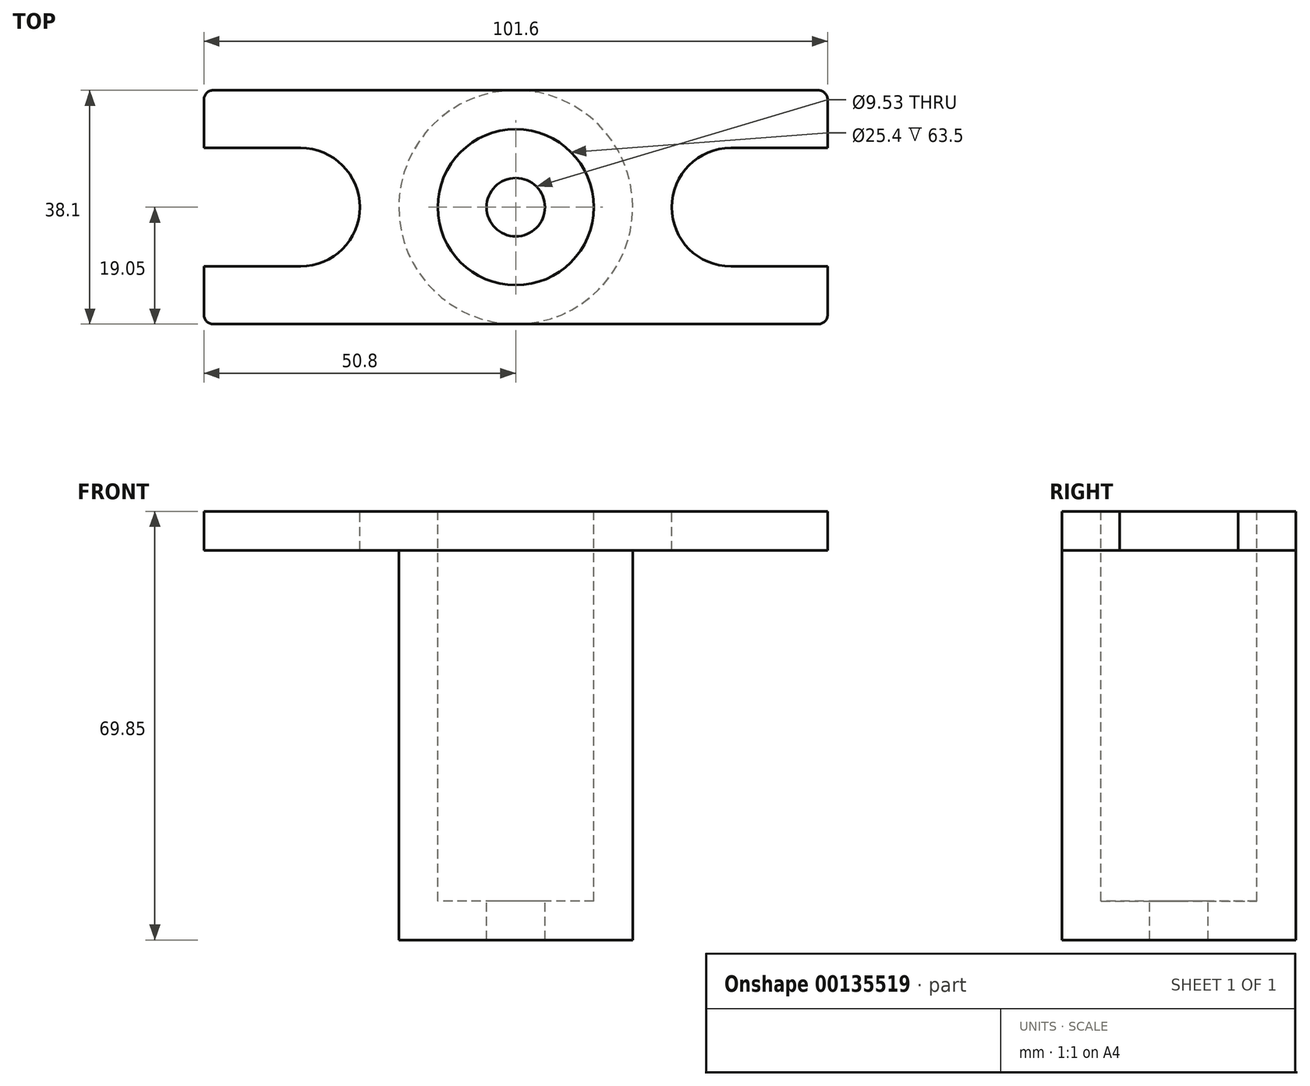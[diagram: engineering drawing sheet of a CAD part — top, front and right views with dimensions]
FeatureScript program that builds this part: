
annotation { "Feature Type Name" : "Feature", "Feature Type Description" : "" }
export const myFeature = defineFeature(function(context is Context, id is Id, definition is map)
    precondition{}
    {
        {
            var Q0;
            Q0=qCreatedBy(makeId("Top.planeOp"),FACE);
            var sketch = newSketch(context, id + "F0", { "sketchPlane" : qUnion([Q0])});
            skCircle(sketch, "E0", {"center": v(0, 0) * mm, "radius": 4.76 * mm});
            skCircle(sketch, "E1", {"center": v(0, 0) * mm, "radius": 19.05 * mm});
            skSolve(sketch);
        }
        {
            var Q0;
            Q0 = qSketchRegion(id + "F0", true);
            extrude(context, id + "F1", {"entities" : qUnion([Q0]), "oppositeDirection" : true, "depth" : 69.85 * mm});
        }
        {
            var Q0;
            Q0=makeQuery(id+"F1.opExtrude","CAP_FACE",FACE,{"disambiguationData":[OSD([sQuery(id+"F0.wireOp",EDGE,"E0"),sQuery(id+"F0.wireOp",EDGE,"E1")])],"isStart":true});
            var sketch = newSketch(context, id + "F2", { "sketchPlane" : qUnion([Q0])});
            skCircle(sketch, "E2", {"center": v(0, 0) * mm, "radius": 12.7 * mm});
            skSolve(sketch);
        }
        {
            var Q0;
            Q0 = qSketchRegion(id + "F2", true);
            extrude(context, id + "F3", {"entities" : qUnion([Q0]), "operationType" : NewBodyOperationType.REMOVE, "oppositeDirection" : true, "depth" : 63.5 * mm});
        }
        {
            var Q0;
            Q0=makeQuery(id+"F1.opExtrude","CAP_FACE",FACE,{"disambiguationData":[OSD([sQuery(id+"F0.wireOp",EDGE,"E0"),sQuery(id+"F0.wireOp",EDGE,"E1")])],"isStart":true});
            var sketch = newSketch(context, id + "F4", { "sketchPlane" : qUnion([Q0])});
            skLineSegment(sketch, "E3.bottom", {"start": v(49.28, -19.05) * mm, "end": v(-49.28, -19.05) * mm});
            skLineSegment(sketch, "E3.top", {"start": v(49.28, 19.05) * mm, "end": v(-49.28, 19.05) * mm});
            skLineSegment(sketch, "E3.left", {"start": v(50.8, -17.53) * mm, "end": v(50.8, 17.53) * mm});
            skLineSegment(sketch, "E3.right", {"start": v(-50.8, -17.53) * mm, "end": v(-50.8, 17.53) * mm});
            skPoint(sketch, "E3.middle", {"position": v(0, 0) * mm});
            skPoint(sketch, "E4.visualSharp", {"position": v(-50.8, 19.05) * mm});
            skArc(sketch, "E4.filletArc", {"start": v(-49.28, 19.05) * mm, "mid": v(-50.35, 18.6) * mm, "end": v(-50.8, 17.53) * mm});
            skPoint(sketch, "E5.visualSharp", {"position": v(50.8, 19.05) * mm});
            skArc(sketch, "E5.filletArc", {"start": v(50.8, 17.53) * mm, "mid": v(50.35, 18.6) * mm, "end": v(49.28, 19.05) * mm});
            skPoint(sketch, "E6.visualSharp", {"position": v(50.8, -19.05) * mm});
            skArc(sketch, "E6.filletArc", {"start": v(49.28, -19.05) * mm, "mid": v(50.35, -18.6) * mm, "end": v(50.8, -17.53) * mm});
            skPoint(sketch, "E7.visualSharp", {"position": v(-50.8, -19.05) * mm});
            skArc(sketch, "E7.filletArc", {"start": v(-50.8, -17.53) * mm, "mid": v(-50.35, -18.6) * mm, "end": v(-49.28, -19.05) * mm});
            skCircle(sketch, "E8", {"center": v(0, 0) * mm, "radius": 12.7 * mm});
            skSolve(sketch);
        }
        {
            var Q0;
            Q0 = qSketchRegion(id + "F4", true);
            extrude(context, id + "F5", {"entities" : qUnion([Q0]), "operationType" : NewBodyOperationType.ADD, "oppositeDirection" : true, "depth" : 6.35 * mm});
        }
        {
            var Q0;
            Q0=makeQuery(id+"F5.boolean.opBoolean","MERGE",FACE,{"derivedFrom":[makeQuery(id+"F1.opExtrude","CAP_FACE",FACE,{"disambiguationData":[OSD([sQuery(id+"F0.wireOp",EDGE,"E0"),sQuery(id+"F0.wireOp",EDGE,"E1")])],"isStart":true}),makeQuery(id+"F5.opExtrude","CAP_FACE",FACE,{"disambiguationData":[OSD([sQuery(id+"F4.wireOp",EDGE,"E3.bottom"),sQuery(id+"F4.wireOp",EDGE,"E3.top"),sQuery(id+"F4.wireOp",EDGE,"E3.left"),sQuery(id+"F4.wireOp",EDGE,"E3.right"),sQuery(id+"F4.wireOp",EDGE,"E4.filletArc"),sQuery(id+"F4.wireOp",EDGE,"E5.filletArc"),sQuery(id+"F4.wireOp",EDGE,"E6.filletArc"),sQuery(id+"F4.wireOp",EDGE,"E7.filletArc"),sQuery(id+"F4.wireOp",EDGE,"E8")])],"isStart":true})]});
            var sketch = newSketch(context, id + "F6", { "sketchPlane" : qUnion([Q0])});
            skLineSegment(sketch, "E9", {"start": v(0, 0) * mm, "end": v(-35.05, 0) * mm, "construction": true});
            skLineSegment(sketch, "E10", {"start": v(0, 0) * mm, "end": v(35.05, 0) * mm, "construction": true});
            skArc(sketch, "E11", {"start": v(-35.05, -9.65) * mm, "mid": v(-25.4, 0) * mm, "end": v(-35.05, 9.65) * mm});
            skArc(sketch, "E12", {"start": v(35.05, 9.65) * mm, "mid": v(25.4, 0) * mm, "end": v(35.05, -9.65) * mm});
            skLineSegment(sketch, "E13", {"start": v(-35.05, -9.65) * mm, "end": v(-50.8, -9.65) * mm});
            skLineSegment(sketch, "E14", {"start": v(-35.05, 9.65) * mm, "end": v(-50.8, 9.65) * mm});
            skLineSegment(sketch, "E15", {"start": v(35.05, -9.65) * mm, "end": v(50.8, -9.65) * mm});
            skLineSegment(sketch, "E16", {"start": v(35.05, 9.65) * mm, "end": v(50.8, 9.65) * mm});
            skLineSegment(sketch, "E17", {"start": v(50.8, 9.65) * mm, "end": v(50.8, -9.65) * mm});
            skSolve(sketch);
        }
        {
            var Q0;
            Q0=makeQuery(id+"F6.imprint","IMPRINT",FACE,{"disambiguationData":[TD([[makeQuery(id+"F6.imprint","IMPRINT",EDGE,{"derivedFrom":sQuery(id+"F6.wireOp",EDGE,"E12")}),1.0]])]});
            var Q1;
            Q1=makeQuery(id+"F6.imprint","IMPRINT",FACE,{"disambiguationData":[TD([[makeQuery(id+"F6.imprint","IMPRINT",EDGE,{"derivedFrom":sQuery(id+"F6.wireOp",EDGE,"E11")}),1.0]])]});
            var Q2;
            {var subQ0=sQuery(id+"F4.wireOp",EDGE,"E3.bottom");var subQ1=sQuery(id+"F4.wireOp",EDGE,"E3.top");var subQ2=sQuery(id+"F4.wireOp",EDGE,"E7.filletArc");var subQ3=sQuery(id+"F4.wireOp",EDGE,"E4.filletArc");var subQ4=sQuery(id+"F4.wireOp",EDGE,"E3.right");var subQ5=makeQuery(id+"F5.opExtrude","CAP_FACE",FACE,{"disambiguationData":[OSD([subQ0,subQ1,sQuery(id+"F4.wireOp",EDGE,"E3.left"),subQ4,subQ3,sQuery(id+"F4.wireOp",EDGE,"E5.filletArc"),sQuery(id+"F4.wireOp",EDGE,"E6.filletArc"),subQ2,sQuery(id+"F4.wireOp",EDGE,"E8")])],"isStart":false});Q2=makeQuery(id+"F5.boolean.opBoolean","SPLIT",FACE,{"disambiguationData":[TD([makeQuery(id+"F5.opExtrude","SWEPT_FACE",FACE,{"disambiguationData":[OSD([subQ4])]})])],"derivedFrom":subQ5});}
            extrude(context, id + "F7", {"entities" : qUnion([Q0, Q1]), "operationType" : NewBodyOperationType.REMOVE, "endBound" : BoundingType.UP_TO_SURFACE, "oppositeDirection" : true, "endBoundEntityFace" : qUnion([Q2]), "depth" : 25.4 * mm});
        }
    });
